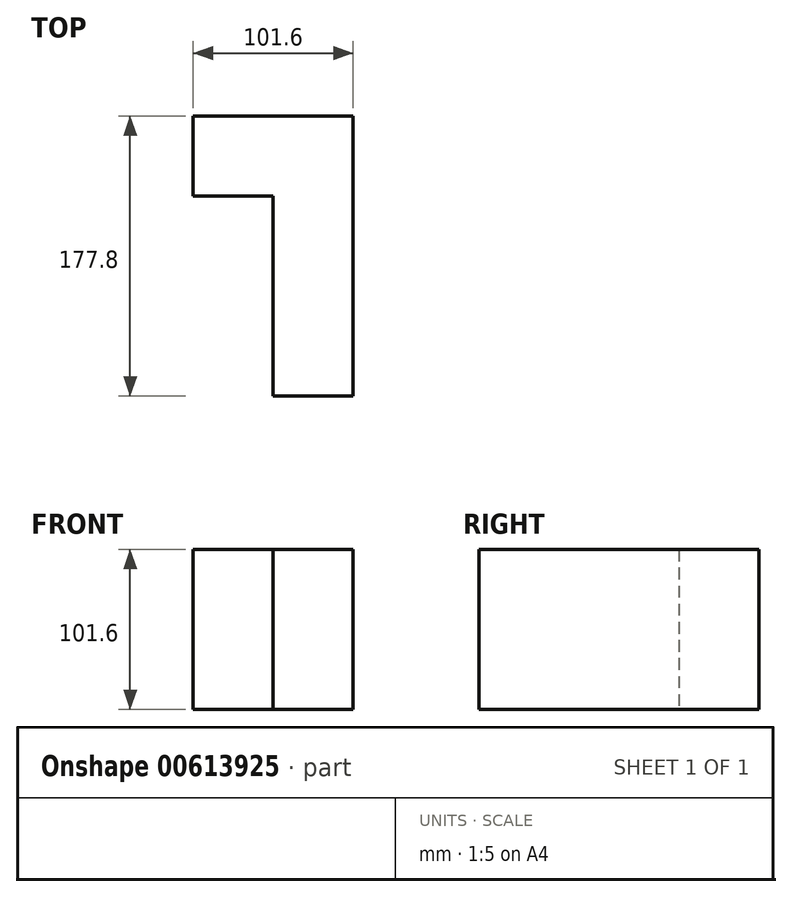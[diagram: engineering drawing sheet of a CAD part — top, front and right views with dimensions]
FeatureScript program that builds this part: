
annotation { "Feature Type Name" : "Feature", "Feature Type Description" : "" }
export const myFeature = defineFeature(function(context is Context, id is Id, definition is map)
    precondition{}
    {
        {
            var Q0;
            Q0=qCreatedBy(makeId("Top.planeOp"),FACE);
            var sketch = newSketch(context, id + "F0", { "sketchPlane" : qUnion([Q0])});
            skLineSegment(sketch, "E0.bottom", {"start": v(-32.67, 101.8) * mm, "end": v(68.93, 101.8) * mm});
            skLineSegment(sketch, "E0.top", {"start": v(-32.67, 51) * mm, "end": v(68.93, 51) * mm});
            skLineSegment(sketch, "E0.left", {"start": v(-32.67, 101.8) * mm, "end": v(-32.67, 51) * mm});
            skLineSegment(sketch, "E0.right", {"start": v(68.93, 101.8) * mm, "end": v(68.93, 51) * mm});
            skLineSegment(sketch, "E1.bottom", {"start": v(68.93, 101.8) * mm, "end": v(18.13, 101.8) * mm});
            skLineSegment(sketch, "E1.top", {"start": v(68.93, -76) * mm, "end": v(18.13, -76) * mm});
            skLineSegment(sketch, "E1.left", {"start": v(68.93, 101.8) * mm, "end": v(68.93, -76) * mm});
            skLineSegment(sketch, "E1.right", {"start": v(18.13, 101.8) * mm, "end": v(18.13, -76) * mm});
            skSolve(sketch);
        }
        {
            var Q0;
            Q0 = qSketchRegion(id + "F0", true);
            extrude(context, id + "F1", {"entities" : qUnion([Q0]), "depth" : 101.6 * mm, "offsetDistance" : 25.4 * mm});
        }
    });
